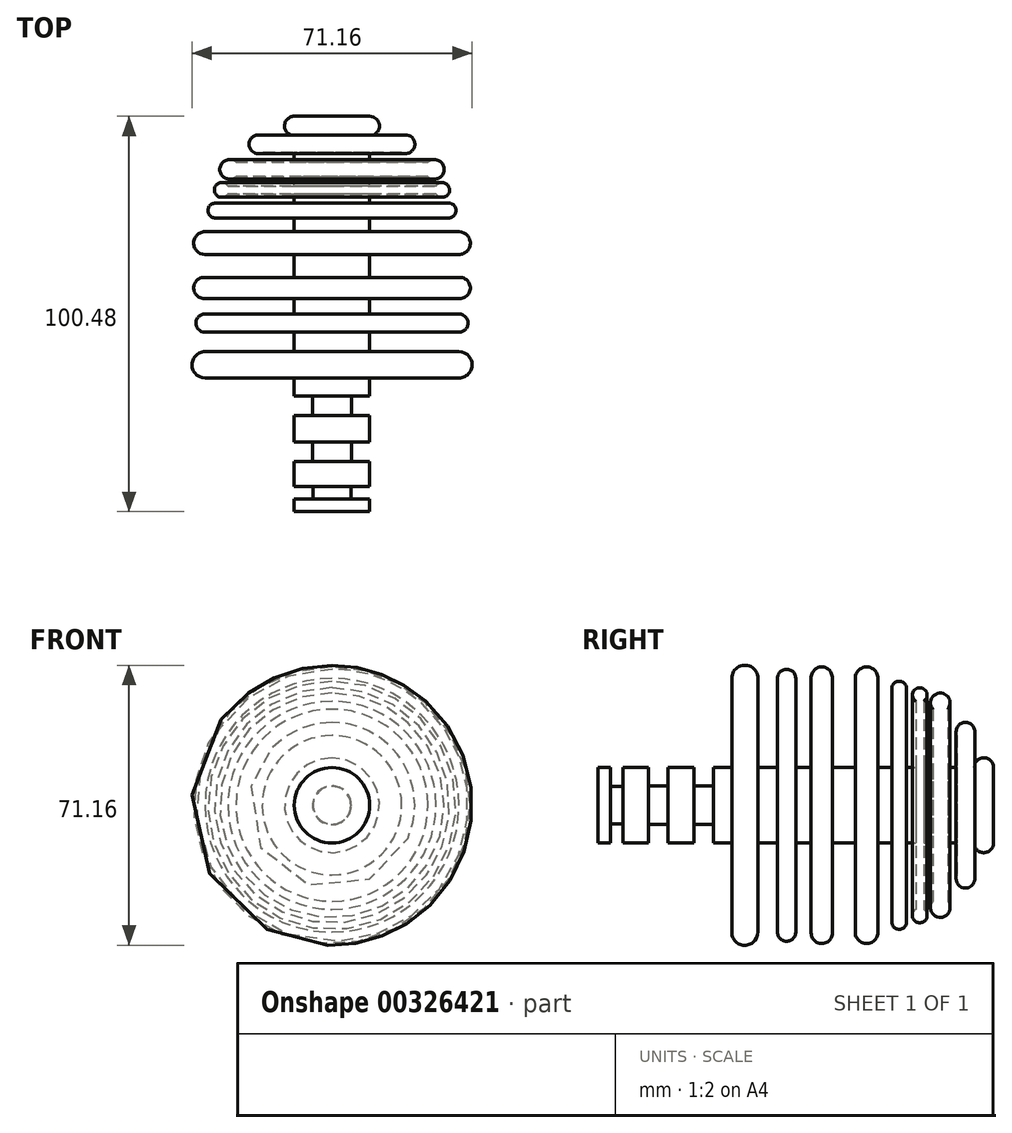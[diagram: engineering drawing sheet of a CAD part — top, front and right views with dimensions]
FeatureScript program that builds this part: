
annotation { "Feature Type Name" : "Feature", "Feature Type Description" : "" }
export const myFeature = defineFeature(function(context is Context, id is Id, definition is map)
    precondition{}
    {
        {
            var Q0;
            Q0=qCreatedBy(makeId("Top.planeOp"),FACE);
            var sketch = newSketch(context, id + "F0", { "sketchPlane" : qUnion([Q0])});
            skLineSegment(sketch, "E0", {"start": v(0, 46.32) * mm, "end": v(0, 5.37) * mm});
            skLineSegment(sketch, "E1.bottom", {"start": v(0, -54.16) * mm, "end": v(-9.58, -54.16) * mm});
            skLineSegment(sketch, "E1.left", {"start": v(0, -54.16) * mm, "end": v(0, -20.18) * mm});
            skLineSegment(sketch, "E1.right", {"start": v(-9.58, -54.16) * mm, "end": v(-9.58, -50.97) * mm});
            skLineSegment(sketch, "E2.bottom", {"start": v(-9.58, -20.18) * mm, "end": v(-32.24, -20.18) * mm});
            skLineSegment(sketch, "E2.top", {"start": v(-9.58, -13.5) * mm, "end": v(-32.24, -13.5) * mm});
            skLineSegment(sketch, "E2.left", {"start": v(0, -20.18) * mm, "end": v(0, -13.5) * mm});
            skLineSegment(sketch, "E2.right", {"start": v(-32.24, -20.18) * mm, "end": v(-32.24, -13.5) * mm});
            skLineSegment(sketch, "E3.bottom", {"start": v(-9.58, -3.92) * mm, "end": v(-32.24, -3.92) * mm});
            skLineSegment(sketch, "E3.top", {"start": v(-9.58, -8.57) * mm, "end": v(-32.24, -8.57) * mm});
            skLineSegment(sketch, "E3.left", {"start": v(0, -3.92) * mm, "end": v(0, -8.57) * mm});
            skLineSegment(sketch, "E3.right", {"start": v(-32.24, -3.92) * mm, "end": v(-32.24, -8.57) * mm});
            skLineSegment(sketch, "E4.bottom", {"start": v(-9.58, 0) * mm, "end": v(-32.24, 0) * mm});
            skLineSegment(sketch, "E4.top", {"start": v(-9.58, 5.37) * mm, "end": v(-32.24, 5.37) * mm});
            skLineSegment(sketch, "E4.left", {"start": v(0, 0) * mm, "end": v(0, 5.37) * mm});
            skLineSegment(sketch, "E4.right", {"start": v(-32.24, 0) * mm, "end": v(-32.24, 5.37) * mm});
            skLineSegment(sketch, "E5.bottom", {"start": v(-9.58, 11.18) * mm, "end": v(-32.24, 11.18) * mm});
            skLineSegment(sketch, "E5.top", {"start": v(-9.58, 16.99) * mm, "end": v(-32.24, 16.99) * mm});
            skLineSegment(sketch, "E5.left", {"start": v(0, 11.18) * mm, "end": v(0, 16.99) * mm});
            skLineSegment(sketch, "E5.right", {"start": v(-32.24, 11.18) * mm, "end": v(-32.24, 16.99) * mm});
            skLineSegment(sketch, "E6.bottom", {"start": v(-9.58, 24.25) * mm, "end": v(-29.62, 24.25) * mm});
            skLineSegment(sketch, "E6.top", {"start": v(-9.58, 20.47) * mm, "end": v(-29.62, 20.47) * mm});
            skLineSegment(sketch, "E6.left", {"start": v(0, 24.25) * mm, "end": v(0, 20.47) * mm});
            skLineSegment(sketch, "E6.right", {"start": v(-29.62, 24.25) * mm, "end": v(-29.62, 20.47) * mm});
            skLineSegment(sketch, "E7.bottom", {"start": v(-9.58, 34.7) * mm, "end": v(-24.4, 34.7) * mm});
            skLineSegment(sketch, "E7.top", {"start": v(-9.58, 30.93) * mm, "end": v(-24.4, 30.93) * mm});
            skLineSegment(sketch, "E7.left", {"start": v(0, 34.7) * mm, "end": v(0, 30.93) * mm});
            skLineSegment(sketch, "E7.right", {"start": v(-24.4, 34.7) * mm, "end": v(-24.4, 30.93) * mm});
            skLineSegment(sketch, "E8.bottom", {"start": v(-9.58, 28.6) * mm, "end": v(-26.43, 28.6) * mm});
            skLineSegment(sketch, "E8.top", {"start": v(-9.58, 26.57) * mm, "end": v(-26.43, 26.57) * mm});
            skLineSegment(sketch, "E8.left", {"start": v(0, 28.6) * mm, "end": v(0, 26.57) * mm});
            skLineSegment(sketch, "E8.right", {"start": v(-26.43, 28.6) * mm, "end": v(-26.43, 26.57) * mm});
            skLineSegment(sketch, "E9.bottom", {"start": v(0, 41.38) * mm, "end": v(-17.72, 41.38) * mm});
            skLineSegment(sketch, "E9.top", {"start": v(-9.58, 37.03) * mm, "end": v(-17.72, 37.03) * mm});
            skLineSegment(sketch, "E9.left", {"start": v(0, 41.38) * mm, "end": v(0, 37.03) * mm});
            skLineSegment(sketch, "E9.right", {"start": v(-17.72, 41.38) * mm, "end": v(-17.72, 37.03) * mm});
            skLineSegment(sketch, "E10", {"start": v(-9.58, -13.5) * mm, "end": v(-9.58, -8.57) * mm});
            skLineSegment(sketch, "E11.trimOffspring", {"start": v(-9.58, -3.92) * mm, "end": v(-9.58, 0) * mm});
            skLineSegment(sketch, "E12.trimOffspring", {"start": v(-9.58, 16.99) * mm, "end": v(-9.58, 20.47) * mm});
            skLineSegment(sketch, "E13.trimOffspring", {"start": v(0, 0) * mm, "end": v(0, -54.16) * mm});
            skLineSegment(sketch, "E14", {"start": v(-9.58, 5.37) * mm, "end": v(-9.58, 11.18) * mm});
            skLineSegment(sketch, "E15.trimOffspring", {"start": v(-9.58, 24.25) * mm, "end": v(-9.58, 26.57) * mm});
            skLineSegment(sketch, "E16.trimOffspring", {"start": v(-9.58, 28.6) * mm, "end": v(-9.58, 30.93) * mm});
            skLineSegment(sketch, "E17.trimOffspring", {"start": v(-9.58, 34.7) * mm, "end": v(-9.58, 37.03) * mm});
            skArc(sketch, "E18", {"start": v(-17.72, 41.38) * mm, "mid": v(-21.06, 39.2) * mm, "end": v(-17.72, 37.03) * mm});
            skArc(sketch, "E19", {"start": v(-24.4, 34.7) * mm, "mid": v(-28.5, 32.82) * mm, "end": v(-24.4, 30.93) * mm});
            skArc(sketch, "E20", {"start": v(-26.43, 28.6) * mm, "mid": v(-29.87, 27.59) * mm, "end": v(-26.43, 26.57) * mm});
            skArc(sketch, "E21", {"start": v(-29.62, 24.25) * mm, "mid": v(-31.51, 22.36) * mm, "end": v(-29.62, 20.47) * mm});
            skArc(sketch, "E22", {"start": v(-32.24, 16.99) * mm, "mid": v(-35.14, 14.09) * mm, "end": v(-32.24, 11.18) * mm});
            skArc(sketch, "E23", {"start": v(-32.24, 5.37) * mm, "mid": v(-35.14, 2.69) * mm, "end": v(-32.24, 0) * mm});
            skPoint(sketch, "E23.midSnap0", {"position": v(-32.24, 2.69) * mm});
            skPoint(sketch, "E23.midSnap1", {"position": v(-35.14, 14.09) * mm});
            skArc(sketch, "E24", {"start": v(-32.24, -3.92) * mm, "mid": v(-34.56, -6.24) * mm, "end": v(-32.24, -8.57) * mm});
            skArc(sketch, "E25", {"start": v(-32.24, -13.5) * mm, "mid": v(-35.58, -16.84) * mm, "end": v(-32.24, -20.18) * mm});
            skLineSegment(sketch, "E26", {"start": v(0, 46.32) * mm, "end": v(-9.58, 46.32) * mm});
            skArc(sketch, "E27", {"start": v(-9.58, 46.32) * mm, "mid": v(-12.05, 43.85) * mm, "end": v(-9.58, 41.38) * mm});
            skPoint(sketch, "E27.endSnap0", {"position": v(-8.86, 41.38) * mm});
            skLineSegment(sketch, "E28", {"start": v(-9.58, -24.83) * mm, "end": v(-4.93, -24.83) * mm});
            skLineSegment(sketch, "E29", {"start": v(-4.93, -24.83) * mm, "end": v(-4.93, -29.77) * mm});
            skLineSegment(sketch, "E30", {"start": v(-4.93, -29.77) * mm, "end": v(-9.58, -29.77) * mm});
            skLineSegment(sketch, "E31.trimOffspring", {"start": v(-9.58, -24.83) * mm, "end": v(-9.58, -20.18) * mm});
            skLineSegment(sketch, "E32", {"start": v(-9.58, -36.45) * mm, "end": v(-4.93, -36.45) * mm});
            skLineSegment(sketch, "E33", {"start": v(-4.93, -36.45) * mm, "end": v(-4.93, -41.38) * mm});
            skLineSegment(sketch, "E34", {"start": v(-4.93, -41.38) * mm, "end": v(-9.58, -41.38) * mm});
            skLineSegment(sketch, "E35.trimOffspring", {"start": v(-9.58, -36.45) * mm, "end": v(-9.58, -29.77) * mm});
            skLineSegment(sketch, "E36", {"start": v(-9.58, -47.77) * mm, "end": v(-4.8, -47.77) * mm});
            skPoint(sketch, "E36.endSnap0", {"position": v(-9.58, -47.77) * mm});
            skPoint(sketch, "E36.endSnap1", {"position": v(-4.8, -54.16) * mm});
            skLineSegment(sketch, "E37", {"start": v(-4.8, -47.77) * mm, "end": v(-4.8, -50.97) * mm});
            skLineSegment(sketch, "E38", {"start": v(-4.8, -50.97) * mm, "end": v(-9.58, -50.97) * mm});
            skLineSegment(sketch, "E39.trimOffspring", {"start": v(-9.58, -47.77) * mm, "end": v(-9.58, -41.38) * mm});
            skSolve(sketch);
        }
        {
            var Q0;
            Q0 = qSketchRegion(id + "F0", true);
            var Q1;
            Q1=sQuery(id+"F0.wireOp",EDGE,"E0");
            revolve(context, id + "F1", {"entities" : qUnion([Q0]), "axis" : qUnion([Q1]), "revolveType" : RevolveType.FULL});
        }
    });
